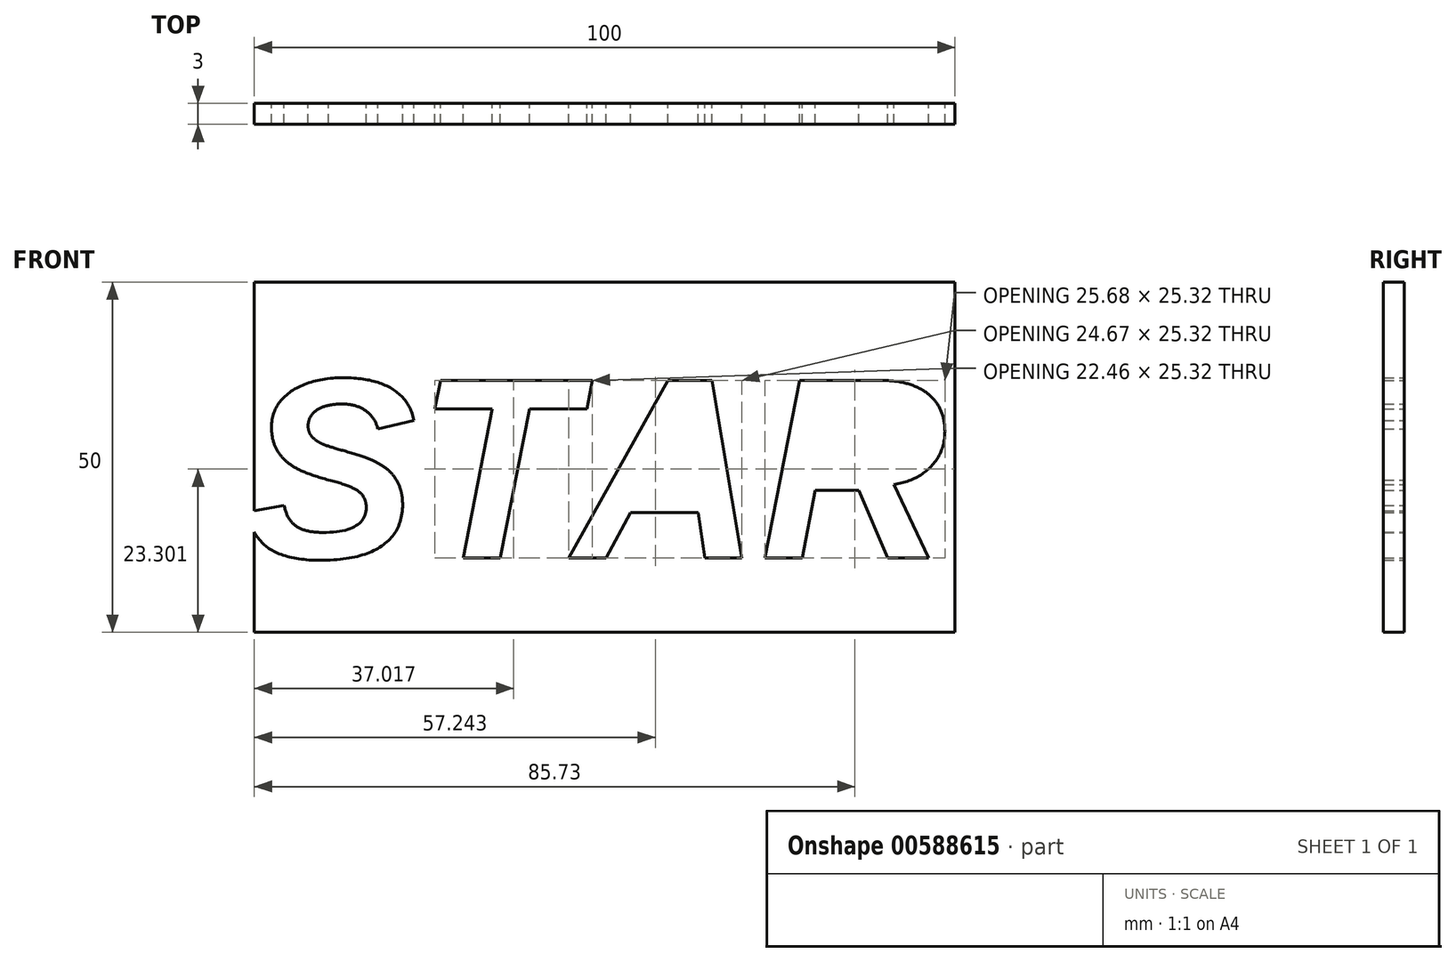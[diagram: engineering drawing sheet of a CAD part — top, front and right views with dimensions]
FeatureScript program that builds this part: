
annotation { "Feature Type Name" : "Feature", "Feature Type Description" : "" }
export const myFeature = defineFeature(function(context is Context, id is Id, definition is map)
    precondition{}
    {
        {
            var Q0;
            Q0=qCreatedBy(makeId("Front.planeOp"),FACE);
            var sketch = newSketch(context, id + "F0", { "sketchPlane" : qUnion([Q0])});
            skLineSegment(sketch, "E0.bottom", {"start": v(0, 0) * mm, "end": v(-100, 0) * mm});
            skLineSegment(sketch, "E0.top", {"start": v(0, 50) * mm, "end": v(-100, 50) * mm});
            skLineSegment(sketch, "E0.left", {"start": v(0, 0) * mm, "end": v(0, 50) * mm});
            skLineSegment(sketch, "E0.right", {"start": v(-100, 0) * mm, "end": v(-100, 50) * mm});
            skText(sketch, "E1", { "text": "STAR", "fontName": "Arimo-BoldItalic.ttf"});
            skLineSegment(sketch, "E2.MirrorCS", {"start": v(0, 100) * mm, "end": v(-100, 100) * mm});
            skLineSegment(sketch, "E3.MirrorCS", {"start": v(0, 100) * mm, "end": v(0, 50) * mm});
            const initialGuessF0  = {"E1": [-0.10137, 0.01064, 1, 0, 0.0265]};
            skSetInitialGuess(sketch, initialGuessF0);
            skSolve(sketch);
        }
        {
            var Q0;
            Q0=makeQuery(id+"F0.imprint","IMPRINT",FACE,{"disambiguationData":[TD([[makeQuery(id+"F0.imprint","IMPRINT",EDGE,{"derivedFrom":sQuery(id+"F0.wireOp",EDGE,"E0.bottom")}),-1.0]])]});
            extrude(context, id + "F1", {"entities" : qUnion([Q0]), "depth" : 3 * mm, "offsetDistance" : 25 * mm});
        }
    });
